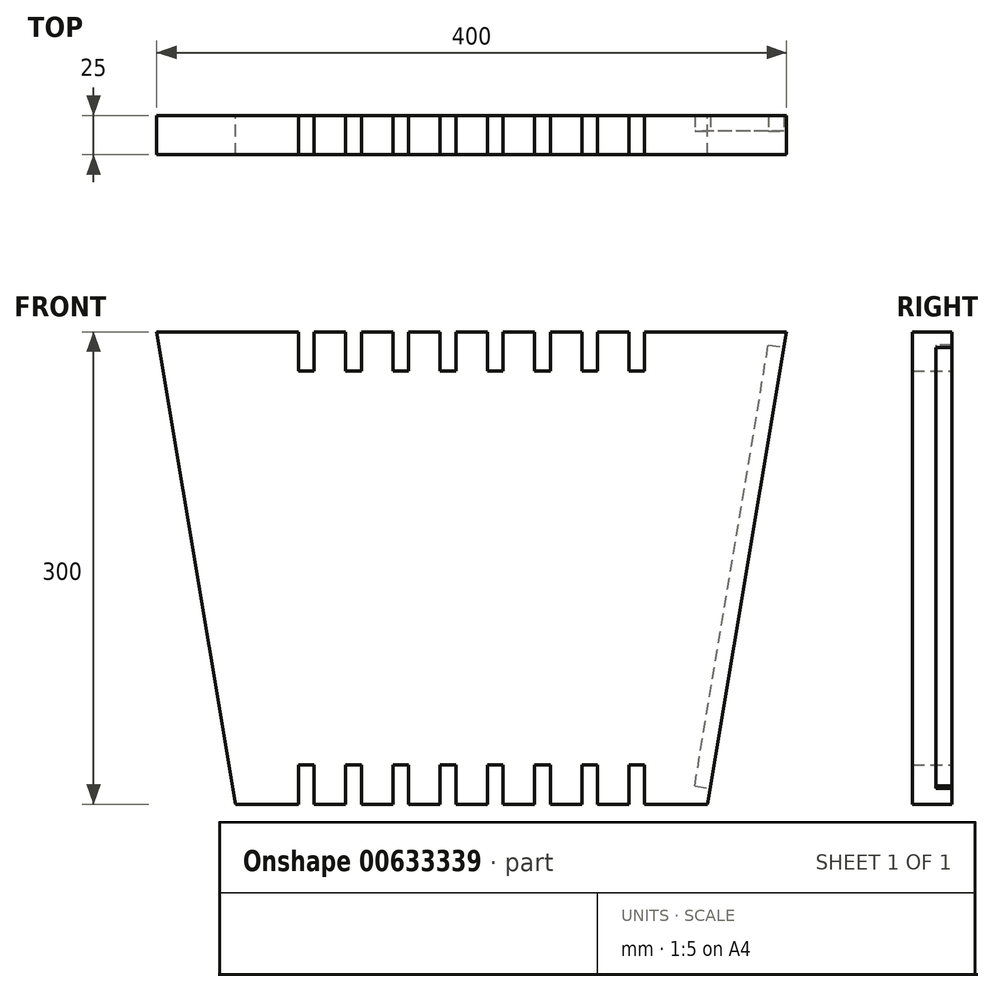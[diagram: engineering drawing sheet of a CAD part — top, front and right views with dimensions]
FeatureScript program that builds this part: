
annotation { "Feature Type Name" : "Feature", "Feature Type Description" : "" }
export const myFeature = defineFeature(function(context is Context, id is Id, definition is map)
    precondition{}
    {
        {
            var Q0;
            Q0=qCreatedBy(makeId("Front.planeOp"),FACE);
            var sketch = newSketch(context, id + "F0", { "sketchPlane" : qUnion([Q0])});
            skLineSegment(sketch, "E0.bottom", {"start": v(150, -150) * mm, "end": v(-150, -150) * mm});
            skPoint(sketch, "E0.middle", {"position": v(0, 0) * mm});
            skLineSegment(sketch, "E1", {"start": v(-200, 150) * mm, "end": v(-150, -150) * mm});
            skLineSegment(sketch, "E2", {"start": v(150, -150) * mm, "end": v(200, 150) * mm});
            skLineSegment(sketch, "E3", {"start": v(-200, 150) * mm, "end": v(200, 150) * mm});
            skLineSegment(sketch, "E4.2.0.1", {"start": v(-70, 150) * mm, "end": v(-80, 150) * mm});
            skLineSegment(sketch, "E4.3.0.0", {"start": v(-110, 150) * mm, "end": v(-110, 125) * mm});
            skLineSegment(sketch, "E4.3.0.1", {"start": v(-100, 150) * mm, "end": v(-110, 150) * mm});
            skLineSegment(sketch, "E4.3.0.2", {"start": v(-100, 125) * mm, "end": v(-110, 125) * mm});
            skLineSegment(sketch, "E4.3.0.3", {"start": v(-100, 150) * mm, "end": v(-100, 125) * mm});
            skLineSegment(sketch, "E5.1.0.0", {"start": v(-80, 150) * mm, "end": v(-80, 125) * mm});
            skLineSegment(sketch, "E5.1.0.2", {"start": v(-70, 125) * mm, "end": v(-80, 125) * mm});
            skLineSegment(sketch, "E5.1.0.3", {"start": v(-70, 150) * mm, "end": v(-70, 125) * mm});
            skLineSegment(sketch, "E5.2.0.0", {"start": v(-50, 150) * mm, "end": v(-50, 125) * mm});
            skLineSegment(sketch, "E5.2.0.1", {"start": v(-40, 150) * mm, "end": v(-50, 150) * mm});
            skLineSegment(sketch, "E5.2.0.2", {"start": v(-40, 125) * mm, "end": v(-50, 125) * mm});
            skLineSegment(sketch, "E5.2.0.3", {"start": v(-40, 150) * mm, "end": v(-40, 125) * mm});
            skLineSegment(sketch, "E5.3.0.0", {"start": v(-20, 150) * mm, "end": v(-20, 125) * mm});
            skLineSegment(sketch, "E5.3.0.1", {"start": v(-10, 150) * mm, "end": v(-20, 150) * mm});
            skLineSegment(sketch, "E5.3.0.2", {"start": v(-10, 125) * mm, "end": v(-20, 125) * mm});
            skLineSegment(sketch, "E5.3.0.3", {"start": v(-10, 150) * mm, "end": v(-10, 125) * mm});
            skLineSegment(sketch, "E5.4.0.0", {"start": v(10, 150) * mm, "end": v(10, 125) * mm});
            skLineSegment(sketch, "E5.4.0.1", {"start": v(20, 150) * mm, "end": v(10, 150) * mm});
            skLineSegment(sketch, "E5.4.0.2", {"start": v(20, 125) * mm, "end": v(10, 125) * mm});
            skLineSegment(sketch, "E5.4.0.3", {"start": v(20, 150) * mm, "end": v(20, 125) * mm});
            skLineSegment(sketch, "E5.5.0.0", {"start": v(40, 150) * mm, "end": v(40, 125) * mm});
            skLineSegment(sketch, "E5.5.0.1", {"start": v(50, 150) * mm, "end": v(40, 150) * mm});
            skLineSegment(sketch, "E5.5.0.2", {"start": v(50, 125) * mm, "end": v(40, 125) * mm});
            skLineSegment(sketch, "E5.5.0.3", {"start": v(50, 150) * mm, "end": v(50, 125) * mm});
            skLineSegment(sketch, "E5.6.0.0", {"start": v(70, 150) * mm, "end": v(70, 125) * mm});
            skLineSegment(sketch, "E5.6.0.1", {"start": v(80, 150) * mm, "end": v(70, 150) * mm});
            skLineSegment(sketch, "E5.6.0.2", {"start": v(80, 125) * mm, "end": v(70, 125) * mm});
            skLineSegment(sketch, "E5.6.0.3", {"start": v(80, 150) * mm, "end": v(80, 125) * mm});
            skLineSegment(sketch, "E6", {"start": v(-175, 0) * mm, "end": v(175, 0) * mm});
            skLineSegment(sketch, "E7.1.0.0", {"start": v(110, 150) * mm, "end": v(110, 125) * mm});
            skLineSegment(sketch, "E7.1.0.1", {"start": v(100, 150) * mm, "end": v(100, 125) * mm});
            skLineSegment(sketch, "E7.1.0.2", {"start": v(110, 125) * mm, "end": v(100, 125) * mm});
            skLineSegment(sketch, "E8.MirrorCS", {"start": v(-70, -150) * mm, "end": v(-80, -150) * mm});
            skLineSegment(sketch, "E9.MirrorCS", {"start": v(-70, -125) * mm, "end": v(-80, -125) * mm});
            skLineSegment(sketch, "E10.MirrorCS", {"start": v(-100, -125) * mm, "end": v(-110, -125) * mm});
            skLineSegment(sketch, "E11.MirrorCS", {"start": v(-100, -150) * mm, "end": v(-110, -150) * mm});
            skLineSegment(sketch, "E12.MirrorCS", {"start": v(20, -125) * mm, "end": v(10, -125) * mm});
            skLineSegment(sketch, "E13.MirrorCS", {"start": v(-40, -125) * mm, "end": v(-50, -125) * mm});
            skLineSegment(sketch, "E14.MirrorCS", {"start": v(-40, -150) * mm, "end": v(-50, -150) * mm});
            skLineSegment(sketch, "E15.MirrorCS", {"start": v(80, -125) * mm, "end": v(70, -125) * mm});
            skLineSegment(sketch, "E16.MirrorCS", {"start": v(20, -150) * mm, "end": v(10, -150) * mm});
            skLineSegment(sketch, "E17.MirrorCS", {"start": v(80, -150) * mm, "end": v(70, -150) * mm});
            skLineSegment(sketch, "E18.MirrorCS", {"start": v(110, -125) * mm, "end": v(100, -125) * mm});
            skLineSegment(sketch, "E19.MirrorCS", {"start": v(-10, -150) * mm, "end": v(-20, -150) * mm});
            skLineSegment(sketch, "E20.MirrorCS", {"start": v(50, -125) * mm, "end": v(40, -125) * mm});
            skLineSegment(sketch, "E21.MirrorCS", {"start": v(50, -150) * mm, "end": v(40, -150) * mm});
            skLineSegment(sketch, "E22.MirrorCS", {"start": v(-10, -125) * mm, "end": v(-20, -125) * mm});
            skLineSegment(sketch, "E23.MirrorCS", {"start": v(-70, -150) * mm, "end": v(-70, -125) * mm});
            skLineSegment(sketch, "E24.MirrorCS", {"start": v(-40, -150) * mm, "end": v(-40, -125) * mm});
            skLineSegment(sketch, "E25.MirrorCS", {"start": v(-80, -150) * mm, "end": v(-80, -125) * mm});
            skLineSegment(sketch, "E26.MirrorCS", {"start": v(-100, -150) * mm, "end": v(-100, -125) * mm});
            skLineSegment(sketch, "E27.MirrorCS", {"start": v(-110, -150) * mm, "end": v(-110, -125) * mm});
            skLineSegment(sketch, "E28.MirrorCS", {"start": v(-50, -150) * mm, "end": v(-50, -125) * mm});
            skLineSegment(sketch, "E29.MirrorCS", {"start": v(10, -150) * mm, "end": v(10, -125) * mm});
            skLineSegment(sketch, "E30.MirrorCS", {"start": v(50, -150) * mm, "end": v(50, -125) * mm});
            skLineSegment(sketch, "E31.MirrorCS", {"start": v(110, -150) * mm, "end": v(110, -125) * mm});
            skLineSegment(sketch, "E32.MirrorCS", {"start": v(70, -150) * mm, "end": v(70, -125) * mm});
            skLineSegment(sketch, "E33.MirrorCS", {"start": v(40, -150) * mm, "end": v(40, -125) * mm});
            skLineSegment(sketch, "E34.MirrorCS", {"start": v(-10, -150) * mm, "end": v(-10, -125) * mm});
            skLineSegment(sketch, "E35.MirrorCS", {"start": v(80, -150) * mm, "end": v(80, -125) * mm});
            skLineSegment(sketch, "E36.MirrorCS", {"start": v(100, -150) * mm, "end": v(100, -125) * mm});
            skLineSegment(sketch, "E37.MirrorCS", {"start": v(20, -150) * mm, "end": v(20, -125) * mm});
            skLineSegment(sketch, "E38.MirrorCS", {"start": v(-20, -150) * mm, "end": v(-20, -125) * mm});
            skSolve(sketch);
        }
        {
            var Q0;
            {var subQ14=sQuery(id+"F0.wireOp",EDGE,"E1");Q0=makeQuery(id+"F0.imprint","IMPRINT",FACE,{"disambiguationData":[TD([[makeQuery(id+"F0.imprint","IMPRINT",EDGE,{"derivedFrom":subQ14}),1.0]])]});}
            extrude(context, id + "F1", {"entities" : qUnion([Q0]), "depth" : 25 * mm, "offsetDistance" : 25 * mm});
        }
        {
            var Q0;
            Q0=makeQuery(id+"F1.opExtrude","SWEPT_FACE",FACE,{"disambiguationData":[OSD([sQuery(id+"F0.wireOp",EDGE,"E2")])]});
            var sketch = newSketch(context, id + "F2", { "sketchPlane" : qUnion([Q0])});
            skLineSegment(sketch, "E39.bottom", {"start": v(0, 170.84) * mm, "end": v(-10, 170.84) * mm});
            skLineSegment(sketch, "E39.top", {"start": v(0, -113.3) * mm, "end": v(-10, -113.3) * mm});
            skLineSegment(sketch, "E39.left", {"start": v(0, 170.84) * mm, "end": v(0, -113.3) * mm});
            skLineSegment(sketch, "E39.right", {"start": v(-10, 170.84) * mm, "end": v(-10, -113.3) * mm});
            skSolve(sketch);
        }
        {
            var Q0;
            Q0=makeQuery(id+"F2.imprint","IMPRINT",FACE,{"disambiguationData":[TD([[makeQuery(id+"F2.imprint","IMPRINT",EDGE,{"derivedFrom":sQuery(id+"F2.wireOp",EDGE,"E39.bottom")}),1.0]])]});
            extrude(context, id + "F3", {"entities" : qUnion([Q0]), "operationType" : NewBodyOperationType.REMOVE, "oppositeDirection" : true, "depth" : 10 * mm, "offsetDistance" : 25 * mm});
        }
    });
